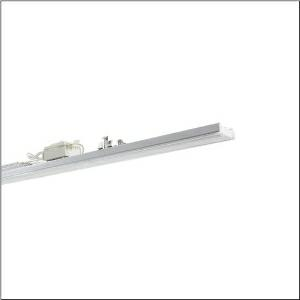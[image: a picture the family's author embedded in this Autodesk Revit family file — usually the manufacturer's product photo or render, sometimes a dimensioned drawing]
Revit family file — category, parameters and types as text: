
# Revit family: licross_r__11_recessed_mo_51te14dv4exg_bf1d
name_source: partatom
category: Lighting Fixtures
units: mm (PartAtom-declared; Revit-internal decimal feet)

## family parameters
Cut with Voids When Loaded = No
Host = Face
Light Source = No
Part Type = Normal
Room Calculation Point = No
Round Connector Dimension = Use Diameter
Shared = No

## types (1)
- --- (1 x LED, 14140 lm, 84.1 W, 4000K)
    Apparent Load = 84 VA
    CIE Flux Codes = 56 84 97 100 100
    Color Rendering = 80
    Color Temperature = 4000K
    Default Elevation = 1800 mm
    Description = Licross® 11 Recessed MO, luminaire insert, of sheet steel, galvanised, coil coated, white, length: 2.250mm, width: 66mm, height: 67mm, LED rated luminous flux: 14.140lm, light colour: 840, control gear: DALI 2, with plug, 5-pole, with phase selection, mains connection: 220..240V, AC, 50/60Hz, rated input power: 84W, halogen-free wiring, primary light control with lens, of plastic, primary optical cover: cover, of PMMA, light emission: direct distribution, primary light characteristic: asymmetric, protection rating (complete): IP54, insulation class (complete): insulation class I (protective earthing), certification: CE, ENEC, VDE, UKCA, protection symbol: D if used in an environment with non-conductive dust loads with corresponding accessories, impact resistance: IK06, permissible ambient temperature for indoor applications: -25..+35°C, corresponds to IFS (International Featured Standards) requirements for safety and quality in the food industry, reducing of maximum allowable ambient temperature of 5°C with ceiling mounting, LABS conformity tested according to VDMA 24364:2018-05, packaging unit: 1 piece
    Height = 58 mm
    Lamp = 1 x LED
    Lamp Light Flux = 14140 lm
    Lamp Power = 84.1 W
    Lamp count = 1
    Length = 2250 mm
    Luminous efficacy = 168 lm/W
    Manufacturer = Siteco
    ModVariant = No
    Model = 51TE14DV4EXG
    Mounting Place = Ceiling
    Mounting Type = Pendant
    Number of Poles = 1
    OnlyDefault = Yes
    Power Factor = 1
    Product Name = Licross® 11 Recessed MO
    Product group = luminaire insert
    ProductGroupID = 902
    Protection Class = Protection class I
    Protection Degree = IP 54
    RLX_Detail_Level = 1
    RLX_Emergency_Light_Flux = 0 lm
    RLX_Emergency_Type = 0
    RLX_Emergency_Type_DB = No
    RlxData = <blob elided: 29945 chars, md5=69f15599>
    Socket = socket
    Standby Power = 0 W
    System Light Flux = 14140 lm
    System Power = 84 W
    Type Comments = factory setting: luminous flux: 100 % | dim-lin: 254 | 378 mA
    Type Image = l_1296930.jpg
    URL = http://relux.com
    VarID = @adj_099982
    Voltage = 0 V
    Weight = 0.00 kg
    Width = 66 mm

## geometry (parser evidence)
native form markers: Blend x4, Sweep x9
no freeform markers — native parametric forms only
